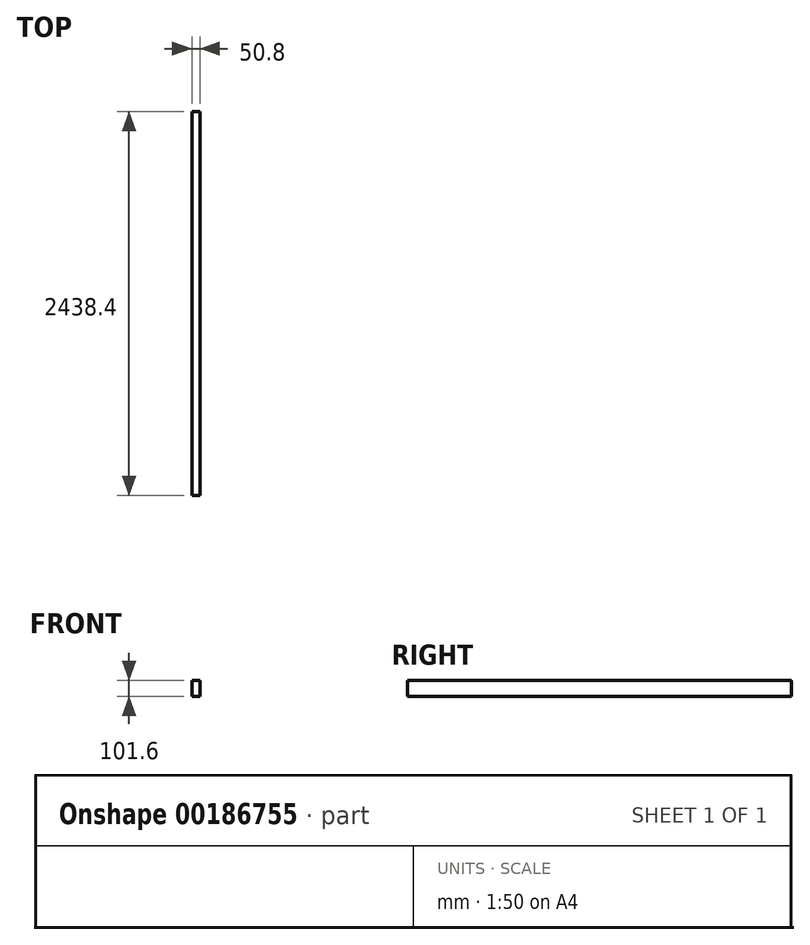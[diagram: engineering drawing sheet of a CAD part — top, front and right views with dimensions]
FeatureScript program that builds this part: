
annotation { "Feature Type Name" : "Feature", "Feature Type Description" : "" }
export const myFeature = defineFeature(function(context is Context, id is Id, definition is map)
    precondition{}
    {
        {
            var Q0;
            Q0=qCreatedBy(makeId("Front.planeOp"),FACE);
            var sketch = newSketch(context, id + "F0", { "sketchPlane" : qUnion([Q0])});
            skLineSegment(sketch, "E0.bottom", {"start": v(-67.79, 123.45) * mm, "end": v(-16.99, 123.45) * mm});
            skLineSegment(sketch, "E0.top", {"start": v(-67.79, 21.85) * mm, "end": v(-16.99, 21.85) * mm});
            skLineSegment(sketch, "E0.left", {"start": v(-67.79, 123.45) * mm, "end": v(-67.79, 21.85) * mm});
            skLineSegment(sketch, "E0.right", {"start": v(-16.99, 123.45) * mm, "end": v(-16.99, 21.85) * mm});
            skSolve(sketch);
        }
        {
            var Q0;
            Q0=makeQuery(id+"F0.imprint","IMPRINT",FACE,{"disambiguationData":[TD([[makeQuery(id+"F0.imprint","IMPRINT",EDGE,{"derivedFrom":sQuery(id+"F0.wireOp",EDGE,"E0.bottom")}),-1.0]])]});
            extrude(context, id + "F1", {"entities" : qUnion([Q0]), "depth" : 2438.4 * mm});
        }
        {
            var Q0;
            Q0=makeQuery(id+"F1.opExtrude","SWEPT_BODY",BODY,{"disambiguationData":[OSD([sQuery(id+"F0.wireOp",EDGE,"E0.bottom"),sQuery(id+"F0.wireOp",EDGE,"E0.top"),sQuery(id+"F0.wireOp",EDGE,"E0.left"),sQuery(id+"F0.wireOp",EDGE,"E0.right")])]});
            transform(context, id + "F2", {"entities" : qUnion([Q0]), "transformType" : TransformType.COPY});
        }
    });
